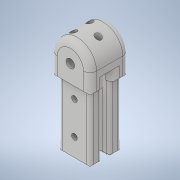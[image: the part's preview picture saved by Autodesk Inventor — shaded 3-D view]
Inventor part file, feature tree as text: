
AUTODESK INVENTOR PART (.ipt)
format: ipt  version: 2020 (Build 240168000, 168)  size: 473,600 bytes
history: native  units: in
note: dims shown in document units (in); Inventor stores cm internally (conversion verified against a paired STEP export)
features: extrude x9, sketch x9, chamfer x6, fillet x4
ambient origin geometry x8: Origin, YZ Plane, XZ Plane, XY Plane, X Axis, Y Axis, Z Axis, Center Point
bodies: Solid1 (feature_tree)
feature tree (28):
  extrude  "Extrusion1"  Depth=1.5in
  fillet  "Fillet1"  Radius=4.0in
  extrude  "Extrusion2"  Depth=0.3281in
  extrude  "Extrusion3"  Depth=0.1562in
  extrude  "Extrusion4"  Depth=2.5156in TaperAngle=0.0deg
  extrude  "Extrusion5"  Depth=0.4375in
  extrude  "Extrusion7"  Depth=0.625in
  extrude  "Extrusion9"  Depth=0.3125in
  chamfer  "Chamfer1"  Distance=1.25in
  chamfer  "Chamfer2"  Distance=0.3in
  chamfer  "Chamfer3"  Distance=0.3in
  fillet  "Fillet2"  Radius=3.125in
  fillet  "Fillet3"  Radius=0.175in
  fillet  "Fillet4"  Radius=0.3in
  chamfer  "Chamfer4"  Distance=0.175in
  extrude  "Extrusion10"  Depth=0.25in
  extrude  "Extrusion11"  Depth=0.25in
  chamfer  "Chamfer5"  Distance=2.5156in
  chamfer  "Chamfer6"  Distance=2.0in
  sketch  "Sketch1"  dims[d0=1.5in d1=1.5in d2=4.0in d3=0.0in]
  sketch  "Sketch2"  dims[d4=0.75in d5=0.3281in]
  sketch  "Sketch3"  dims[d6=4.0in d7=0.0in d8=0.1562in]
  sketch  "Sketch4"  dims[d9=0.1562in d10=2.5156in d11=0.0in]
  sketch  "Sketch5"  dims[d12=0.2313in d13=0.4375in]
  sketch  "Sketch7"  dims[d14=0.0in d15=0.625in]
  sketch  "Sketch10"  dims[d16=0.625in d17=0.3125in]
  sketch  "Sketch12"  dims[d18=0.625in d19=1.25in d20=0.0in]
  sketch  "Sketch14"  dims[d21=0.3in d22=0.3in d23=0.3in d24=3.125in d25=0.0in d26=0.175in d27=0.3in d28=0.175in d29=0.3in d31=0.3in d39=2.5156in d40=0.0in d48=2.0in d49=0.75in d50=0.2188in d53=0.0in d54=0.0in d55=2.5in d56=0.0in d57=0.05in d58=0.125in d59=45.0deg d60=0.0625in d61=0.125in d62=45.0deg d63=0.0625in d64=0.125in d65=45.0deg d66=0.0in d67=0.0in d68=0.125in d69=0.25in d70=0.0625in d71=0.0312in d72=0.125in d73=45.0deg d75=0.125in d76=0.475in d77=0.0in d79=0.3in d80=0.05in d81=0.05in d82=0.35in d83=0.0in d84=0.034in d85=0.125in d86=45.0deg d89=0.05in d90=0.05in d91=0.3in d92=0.025in d93=0.125in d94=45.0deg]
